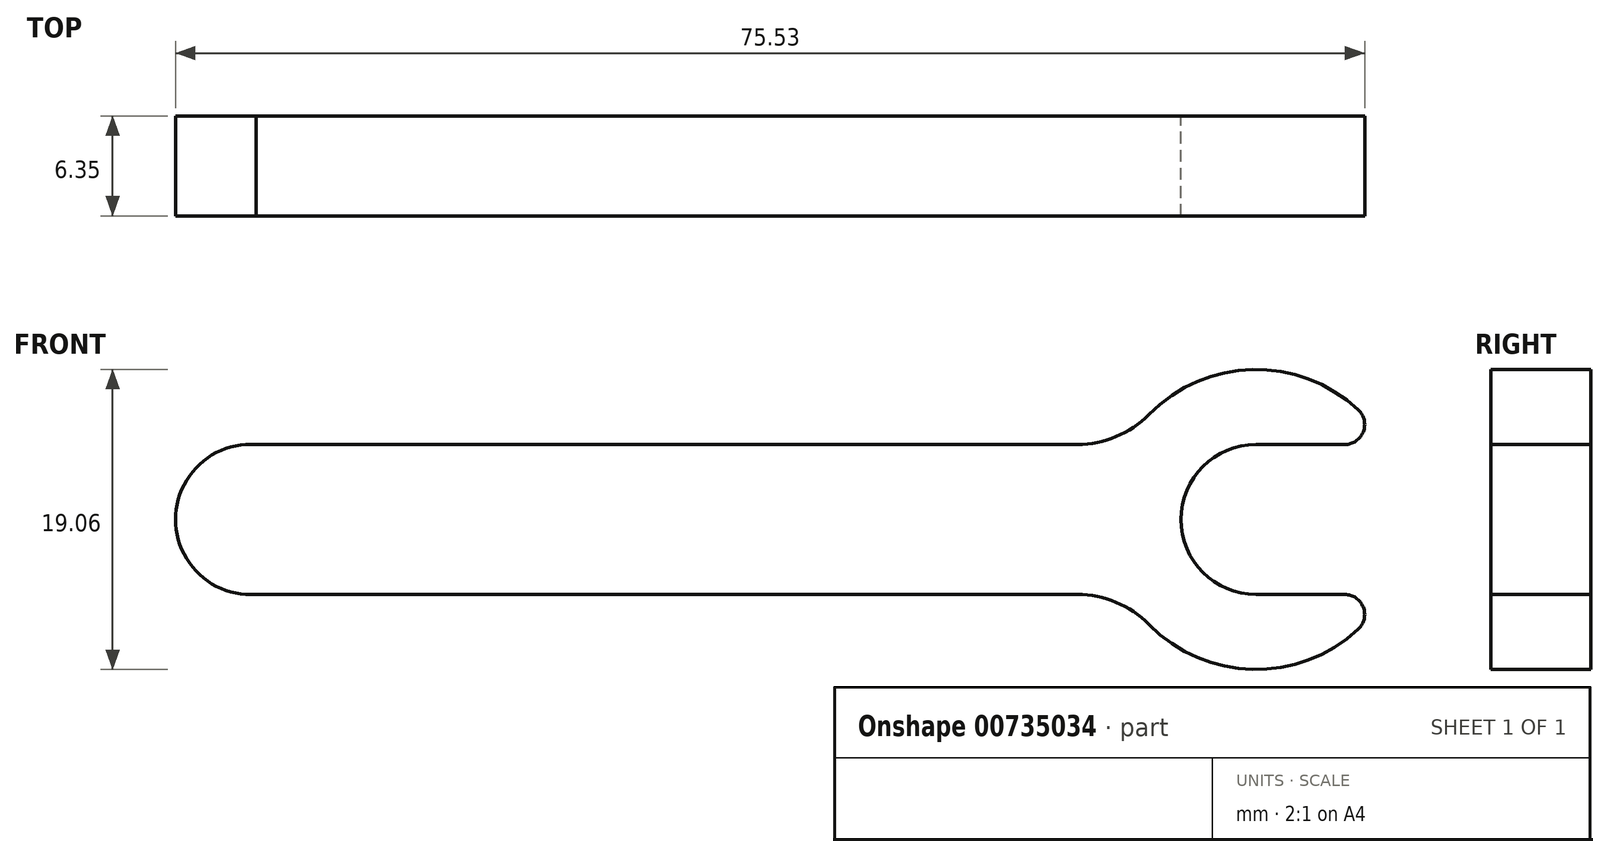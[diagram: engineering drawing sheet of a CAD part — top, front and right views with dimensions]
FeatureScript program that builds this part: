
annotation { "Feature Type Name" : "Feature", "Feature Type Description" : "" }
export const myFeature = defineFeature(function(context is Context, id is Id, definition is map)
    precondition{}
    {
        {
            var Q0;
            Q0=qCreatedBy(makeId("Front.planeOp"),FACE);
            var sketch = newSketch(context, id + "F0", { "sketchPlane" : qUnion([Q0])});
            skLineSegment(sketch, "E0", {"start": v(0, 0) * mm, "end": v(63.5, 0) * mm, "construction": true});
            skLineSegment(sketch, "E1", {"start": v(0, 4.76) * mm, "end": v(52.16, 4.76) * mm});
            skLineSegment(sketch, "E2", {"start": v(0, -4.76) * mm, "end": v(52.16, -4.76) * mm});
            skArc(sketch, "E3", {"start": v(0, 4.76) * mm, "mid": v(-5.12, 0) * mm, "end": v(0, -4.76) * mm});
            skArc(sketch, "E4", {"start": v(56.7, -6.67) * mm, "mid": v(63.3, -9.52) * mm, "end": v(70, -6.96) * mm});
            skLineSegment(sketch, "E5", {"start": v(63.5, -4.76) * mm, "end": v(69.14, -4.76) * mm});
            skLineSegment(sketch, "E6", {"start": v(63.5, 4.76) * mm, "end": v(69.14, 4.76) * mm});
            skArc(sketch, "E7", {"start": v(56.7, -6.67) * mm, "mid": v(54.62, -5.26) * mm, "end": v(52.16, -4.76) * mm});
            skArc(sketch, "E8", {"start": v(70, -6.96) * mm, "mid": v(70.32, -5.57) * mm, "end": v(69.14, -4.76) * mm});
            skArc(sketch, "E9", {"start": v(52.16, 4.76) * mm, "mid": v(54.62, 5.26) * mm, "end": v(56.7, 6.67) * mm});
            skArc(sketch, "E10", {"start": v(70, 6.96) * mm, "mid": v(63.3, 9.52) * mm, "end": v(56.7, 6.67) * mm});
            skArc(sketch, "E11", {"start": v(63.5, 4.76) * mm, "mid": v(58.74, 0) * mm, "end": v(63.5, -4.76) * mm});
            skArc(sketch, "E12", {"start": v(69.14, 4.76) * mm, "mid": v(70.32, 5.57) * mm, "end": v(70, 6.96) * mm});
            skSolve(sketch);
        }
        {
            var Q0;
            Q0 = qSketchRegion(id + "F0", true);
            extrude(context, id + "F1", {"entities" : qUnion([Q0]), "depth" : 6.35 * mm, "offsetDistance" : 25.4 * mm});
        }
    });
